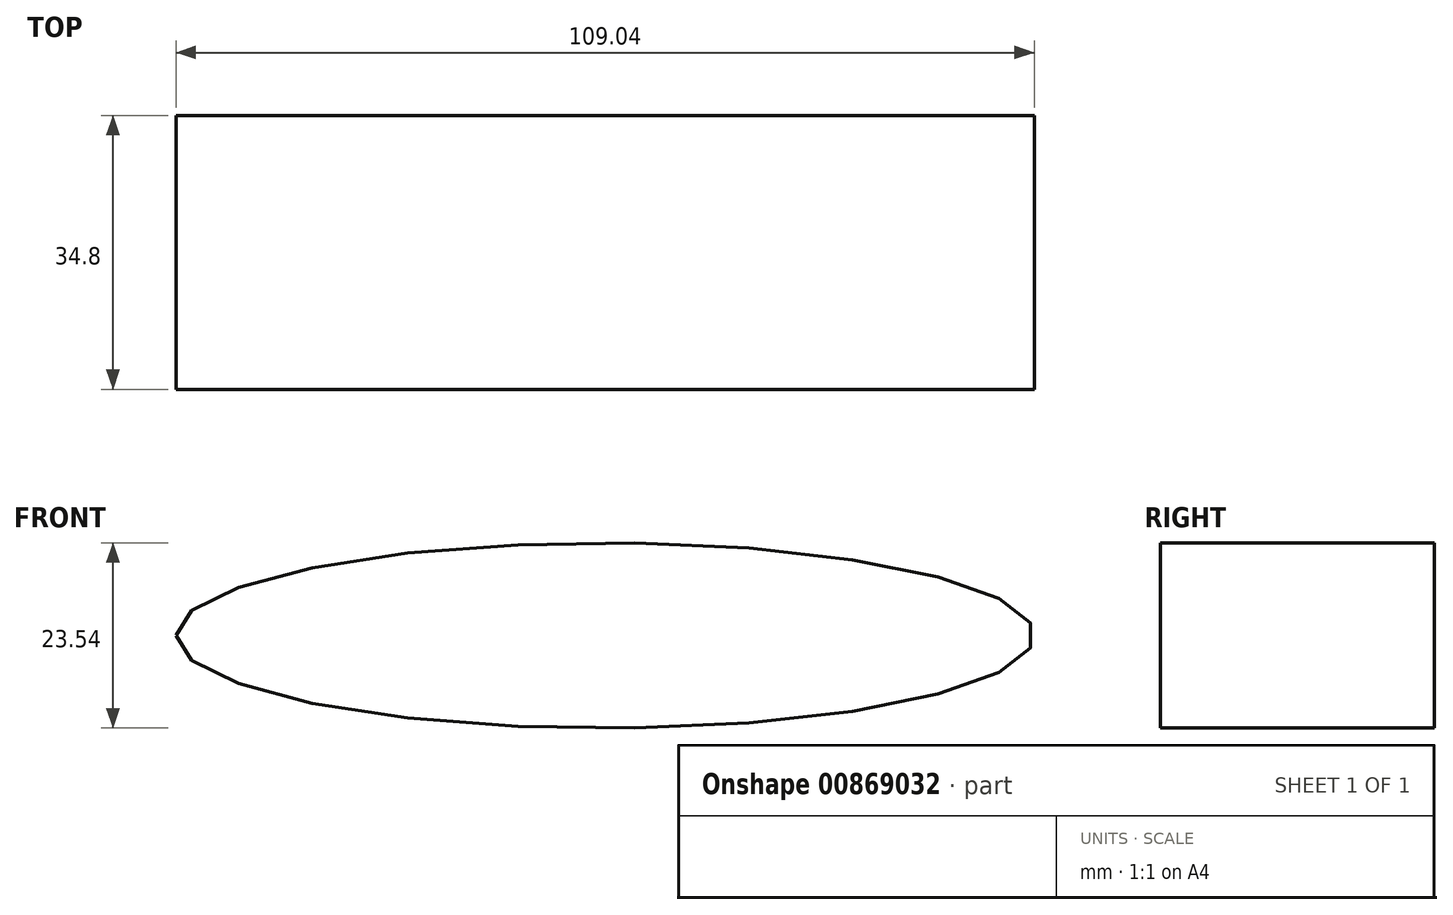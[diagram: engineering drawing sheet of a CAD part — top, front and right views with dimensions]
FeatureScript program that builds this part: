
annotation { "Feature Type Name" : "Feature", "Feature Type Description" : "" }
export const myFeature = defineFeature(function(context is Context, id is Id, definition is map)
    precondition{}
    {
        {
            var Q0;
            Q0=qCreatedBy(makeId("Front.planeOp"),FACE);
            var sketch = newSketch(context, id + "F0", { "sketchPlane" : qUnion([Q0])});
            skEllipse(sketch, "E0", {"center": v(0, 0) * mm, "majorRadius": 54.52 * mm, "minorRadius": 11.77 * mm, "majorAxis": v(-1, 0)});
            skSolve(sketch);
        }
        {
            var Q0;
            Q0 = qSketchRegion(id + "F0", true);
            extrude(context, id + "F1", {"entities" : qUnion([Q0]), "depth" : 34.8 * mm, "offsetDistance" : 25.4 * mm});
        }
    });
